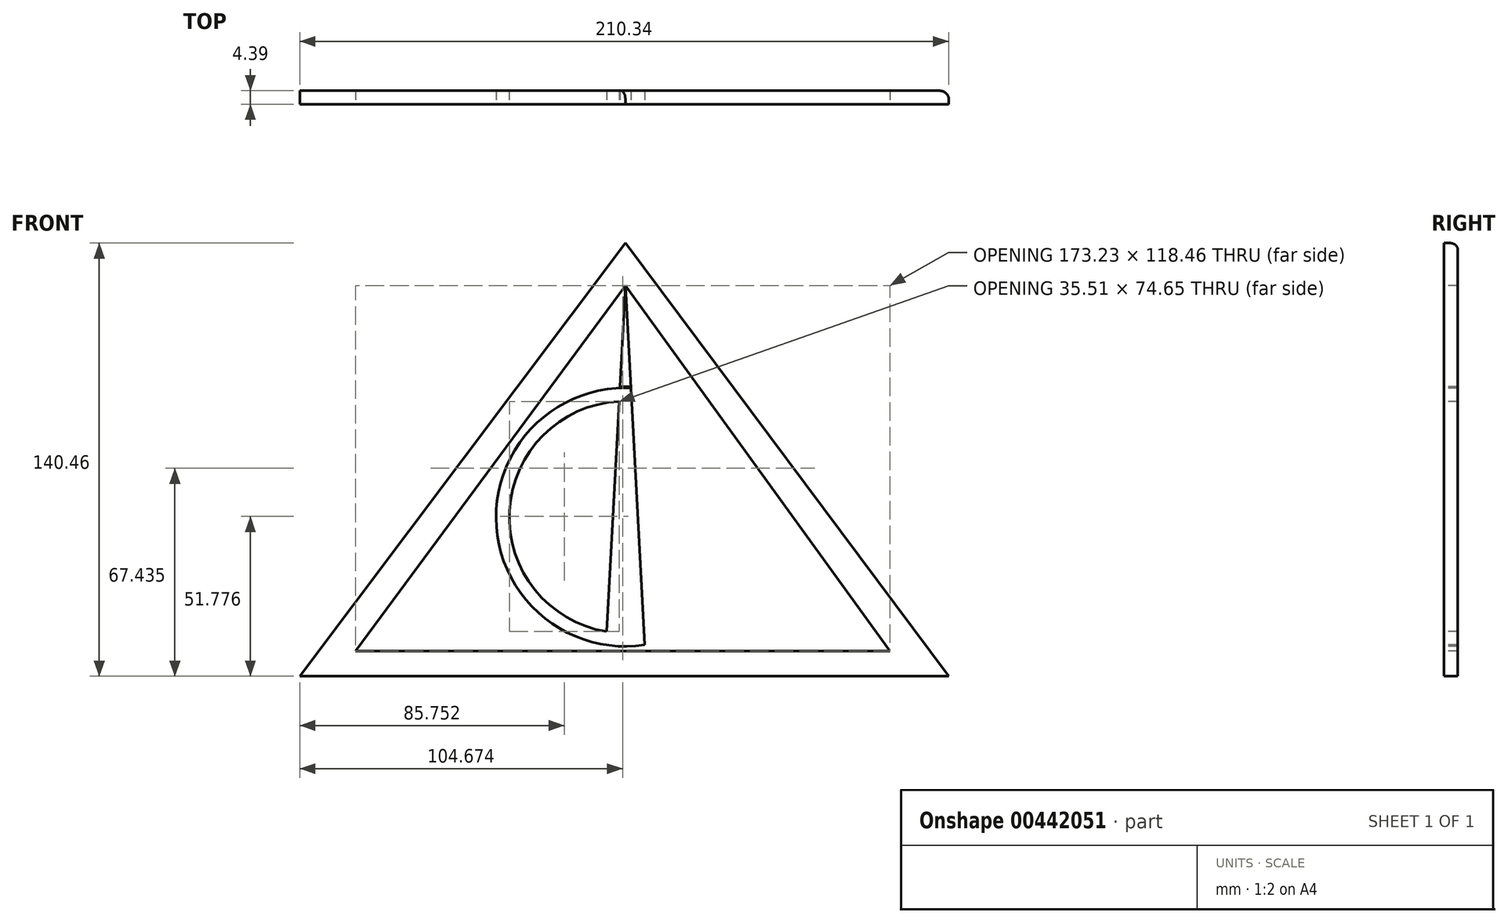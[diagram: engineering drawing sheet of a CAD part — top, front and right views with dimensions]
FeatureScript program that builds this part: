
annotation { "Feature Type Name" : "Feature", "Feature Type Description" : "" }
export const myFeature = defineFeature(function(context is Context, id is Id, definition is map)
    precondition{}
    {
        {
            var Q0;
            Q0=qCreatedBy(makeId("Front.planeOp"),FACE);
            var sketch = newSketch(context, id + "F0", { "sketchPlane" : qUnion([Q0])});
            skLineSegment(sketch, "E0", {"start": v(0, 96.8) * mm, "end": v(-87.48, -21.65) * mm});
            skLineSegment(sketch, "E1", {"start": v(-87.48, -21.65) * mm, "end": v(85.75, -21.65) * mm});
            skLineSegment(sketch, "E2", {"start": v(85.75, -21.65) * mm, "end": v(0, 96.8) * mm});
            skCircle(sketch, "E3", {"center": v(0, 21.7) * mm, "radius": 41.9 * mm});
            skCircle(sketch, "E4", {"center": v(0, 21.7) * mm, "radius": 42.37 * mm});
            skLineSegment(sketch, "E5", {"start": v(0, 96.8) * mm, "end": v(0, -20.2) * mm});
            skLineSegment(sketch, "E6", {"start": v(0, -20.2) * mm, "end": v(6.34, -20.2) * mm});
            skLineSegment(sketch, "E7", {"start": v(6.34, -20.2) * mm, "end": v(0, 96.8) * mm});
            skLineSegment(sketch, "E8", {"start": v(0, 96.8) * mm, "end": v(-6.34, -20.2) * mm});
            skLineSegment(sketch, "E9", {"start": v(-6.34, -20.2) * mm, "end": v(6.34, -20.2) * mm});
            skCircle(sketch, "E10", {"center": v(0, 21.7) * mm, "radius": 37.6 * mm});
            skLineSegment(sketch, "E11", {"start": v(0, 110.6) * mm, "end": v(-105.54, -29.86) * mm});
            skLineSegment(sketch, "E12", {"start": v(-105.54, -29.86) * mm, "end": v(104.8, -29.86) * mm});
            skLineSegment(sketch, "E13", {"start": v(104.8, -29.86) * mm, "end": v(0, 110.6) * mm});
            skSolve(sketch);
        }
        {
            var Q0;
            {var subQ0=sQuery(id+"F0.wireOp",EDGE,"E7");var subQ1=sQuery(id+"F0.wireOp",EDGE,"E3");var subQ2=makeQuery(id+"F0.imprint","INTERSECT",VERTEX,{"disambiguationData":[OD(0.0)],"derivedFrom":[subQ1,subQ0]});Q0=makeQuery(id+"F0.imprint","IMPRINT",FACE,{"disambiguationData":[TD([[makeQuery(id+"F0.imprint","IMPRINT",EDGE,{"disambiguationData":[TD([[subQ2,1.0]])],"derivedFrom":subQ1}),1.0]])]});}
            var Q1;
            Q1=makeQuery(id+"F0.imprint","IMPRINT",FACE,{"disambiguationData":[TD([[makeQuery(id+"F0.imprint","IMPRINT",EDGE,{"derivedFrom":sQuery(id+"F0.wireOp",EDGE,"E0")}),-1.0]])]});
            var Q2;
            {var subQ0=sQuery(id+"F0.wireOp",EDGE,"E8");var subQ1=sQuery(id+"F0.wireOp",EDGE,"E3");var subQ2=makeQuery(id+"F0.imprint","INTERSECT",VERTEX,{"disambiguationData":[OD(0.0)],"derivedFrom":[subQ1,subQ0]});Q2=makeQuery(id+"F0.imprint","IMPRINT",FACE,{"disambiguationData":[TD([[makeQuery(id+"F0.imprint","IMPRINT",EDGE,{"disambiguationData":[TD([[subQ2,-1.0]])],"derivedFrom":subQ1}),1.0]])]});}
            var Q3;
            {var subQ1=sQuery(id+"F0.wireOp",EDGE,"E3");var subQ3=sQuery(id+"F0.wireOp",EDGE,"E7");var subQ4=makeQuery(id+"F0.imprint","INTERSECT",VERTEX,{"disambiguationData":[OD(1.0)],"derivedFrom":[subQ1,subQ3]});Q3=makeQuery(id+"F0.imprint","IMPRINT",FACE,{"disambiguationData":[TD([[makeQuery(id+"F0.imprint","IMPRINT",EDGE,{"disambiguationData":[TD([[subQ4,-1.0]])],"derivedFrom":subQ3}),1.0]])]});}
            var Q4;
            {var subQ1=sQuery(id+"F0.wireOp",EDGE,"E3");var subQ3=sQuery(id+"F0.wireOp",EDGE,"E8");var subQ4=makeQuery(id+"F0.imprint","INTERSECT",VERTEX,{"disambiguationData":[OD(1.0)],"derivedFrom":[subQ1,subQ3]});Q4=makeQuery(id+"F0.imprint","IMPRINT",FACE,{"disambiguationData":[TD([[makeQuery(id+"F0.imprint","IMPRINT",EDGE,{"disambiguationData":[TD([[subQ4,1.0]])],"derivedFrom":subQ3}),1.0]])]});}
            var Q5;
            {var subQ0=sQuery(id+"F0.wireOp",EDGE,"E10");var subQ1=sQuery(id+"F0.wireOp",EDGE,"E5");var subQ2=makeQuery(id+"F0.imprint","INTERSECT",VERTEX,{"disambiguationData":[OD(0.0)],"derivedFrom":[subQ1,subQ0]});Q5=makeQuery(id+"F0.imprint","IMPRINT",FACE,{"disambiguationData":[TD([[makeQuery(id+"F0.imprint","IMPRINT",EDGE,{"disambiguationData":[TD([[subQ2,-1.0]])],"derivedFrom":subQ1}),1.0]])]});}
            var Q6;
            {var subQ0=sQuery(id+"F0.wireOp",EDGE,"E10");var subQ1=sQuery(id+"F0.wireOp",EDGE,"E5");var subQ2=makeQuery(id+"F0.imprint","INTERSECT",VERTEX,{"disambiguationData":[OD(0.0)],"derivedFrom":[subQ1,subQ0]});Q6=makeQuery(id+"F0.imprint","IMPRINT",FACE,{"disambiguationData":[TD([[makeQuery(id+"F0.imprint","IMPRINT",EDGE,{"disambiguationData":[TD([[subQ2,-1.0]])],"derivedFrom":subQ1}),-1.0]])]});}
            var Q7;
            {var subQ0=sQuery(id+"F0.wireOp",EDGE,"E5");var subQ1=sQuery(id+"F0.wireOp",EDGE,"E4");var subQ2=makeQuery(id+"F0.imprint","INTERSECT",VERTEX,{"derivedFrom":[subQ1,subQ0]});Q7=makeQuery(id+"F0.imprint","IMPRINT",FACE,{"disambiguationData":[TD([[makeQuery(id+"F0.imprint","IMPRINT",EDGE,{"disambiguationData":[TD([[subQ2,1.0]])],"derivedFrom":subQ1}),-1.0]])]});}
            var Q8;
            {var subQ0=sQuery(id+"F0.wireOp",EDGE,"E5");var subQ1=sQuery(id+"F0.wireOp",EDGE,"E3");var subQ2=makeQuery(id+"F0.imprint","INTERSECT",VERTEX,{"derivedFrom":[subQ1,subQ0]});Q8=makeQuery(id+"F0.imprint","IMPRINT",FACE,{"disambiguationData":[TD([[makeQuery(id+"F0.imprint","IMPRINT",EDGE,{"disambiguationData":[TD([[subQ2,1.0]])],"derivedFrom":subQ1}),1.0]])]});}
            var Q9;
            {var subQ0=sQuery(id+"F0.wireOp",EDGE,"E5");var subQ1=sQuery(id+"F0.wireOp",EDGE,"E3");var subQ2=makeQuery(id+"F0.imprint","INTERSECT",VERTEX,{"derivedFrom":[subQ1,subQ0]});Q9=makeQuery(id+"F0.imprint","IMPRINT",FACE,{"disambiguationData":[TD([[makeQuery(id+"F0.imprint","IMPRINT",EDGE,{"disambiguationData":[TD([[subQ2,-1.0]])],"derivedFrom":subQ1}),1.0]])]});}
            var Q10;
            {var subQ0=sQuery(id+"F0.wireOp",EDGE,"E5");var subQ1=sQuery(id+"F0.wireOp",EDGE,"E4");var subQ2=makeQuery(id+"F0.imprint","INTERSECT",VERTEX,{"derivedFrom":[subQ1,subQ0]});Q10=makeQuery(id+"F0.imprint","IMPRINT",FACE,{"disambiguationData":[TD([[makeQuery(id+"F0.imprint","IMPRINT",EDGE,{"disambiguationData":[TD([[subQ2,-1.0]])],"derivedFrom":subQ1}),-1.0]])]});}
            extrude(context, id + "F1", {"entities" : qUnion([Q0, Q1, Q2, Q3, Q4, Q5, Q6, Q7, Q8, Q9, Q10]), "oppositeDirection" : true, "depth" : 4.4 * mm});
        }
        {
            var Q0;
            Q0=makeQuery(id+"F1.opExtrude","CAP_EDGE",EDGE,{"disambiguationData":[OSD([sQuery(id+"F0.wireOp",EDGE,"E13")])],"isStart":false});
            fillet(context, id + "F2", {"entities" : qUnion([Q0]), "radius" : 2.54 * mm, "tangentPropagation" : true, "allowEdgeOverflow" : false});
        }
        {
            var Q0;
            {var subQ0=sQuery(id+"F0.wireOp",EDGE,"E5");var subQ1=sQuery(id+"F0.wireOp",EDGE,"E3");var subQ2=makeQuery(id+"F0.imprint","INTERSECT",VERTEX,{"derivedFrom":[subQ1,subQ0]});Q0=makeQuery(id+"F0.imprint","IMPRINT",FACE,{"disambiguationData":[TD([[makeQuery(id+"F0.imprint","IMPRINT",EDGE,{"disambiguationData":[TD([[subQ2,-1.0]])],"derivedFrom":subQ1}),-1.0]])]});}
            var Q1;
            {var subQ0=sQuery(id+"F0.wireOp",EDGE,"E5");var subQ1=sQuery(id+"F0.wireOp",EDGE,"E3");var subQ2=makeQuery(id+"F0.imprint","INTERSECT",VERTEX,{"derivedFrom":[subQ1,subQ0]});Q1=makeQuery(id+"F0.imprint","IMPRINT",FACE,{"disambiguationData":[TD([[makeQuery(id+"F0.imprint","IMPRINT",EDGE,{"disambiguationData":[TD([[subQ2,1.0]])],"derivedFrom":subQ1}),-1.0]])]});}
            extrude(context, id + "F3", {"entities" : qUnion([Q0, Q1]), "oppositeDirection" : true, "depth" : 4.32 * mm});
        }
    });
